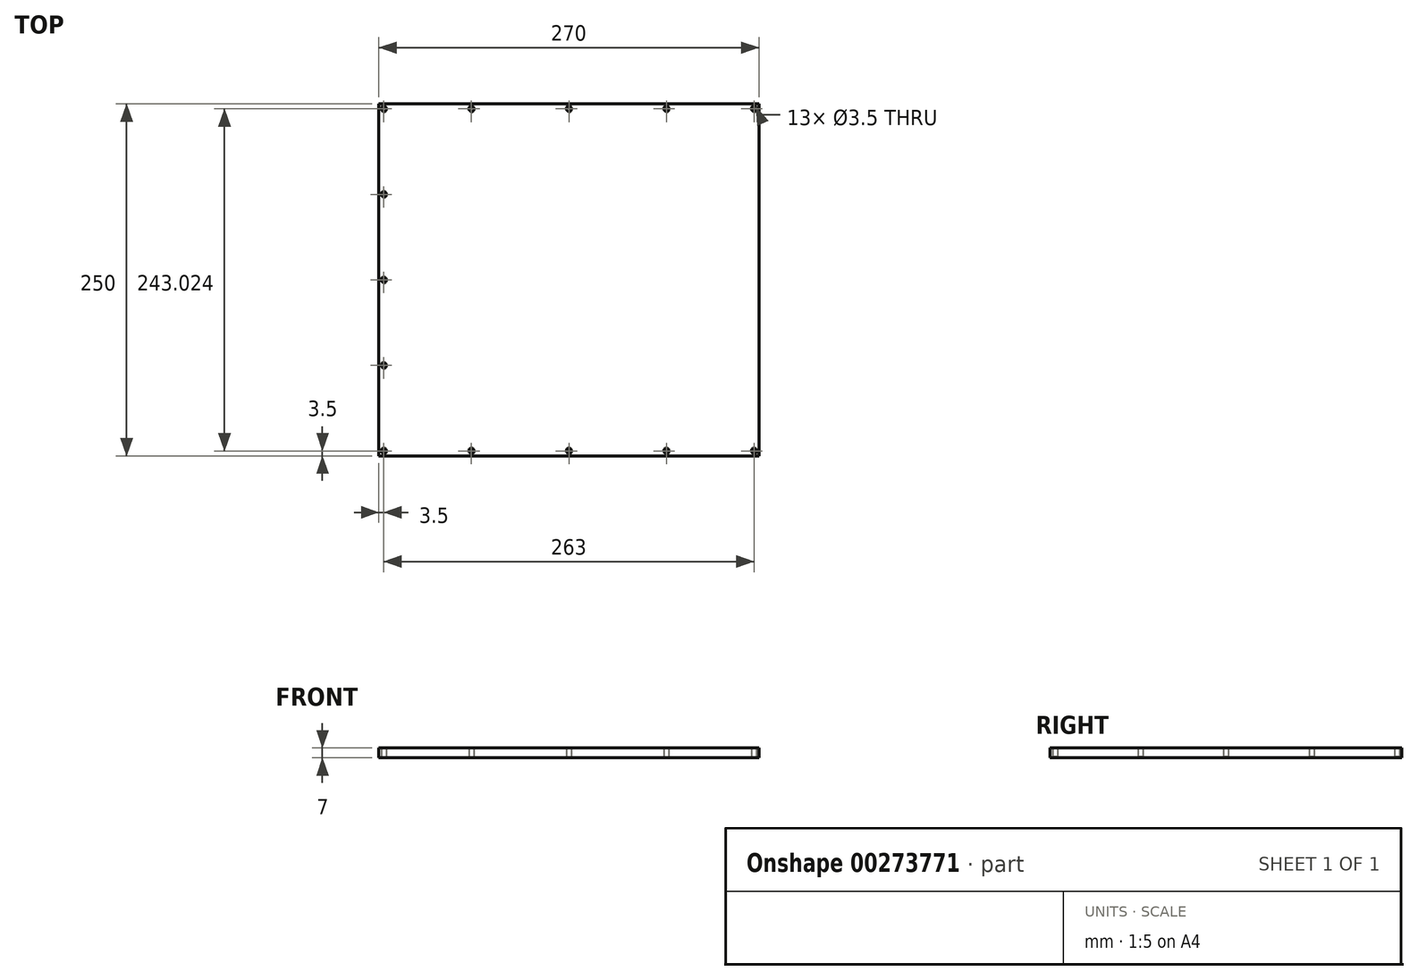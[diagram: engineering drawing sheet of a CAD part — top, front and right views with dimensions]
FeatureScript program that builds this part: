
annotation { "Feature Type Name" : "Feature", "Feature Type Description" : "" }
export const myFeature = defineFeature(function(context is Context, id is Id, definition is map)
    precondition{}
    {
        {
            var Q0;
            Q0=qCreatedBy(makeId("Top.planeOp"),FACE);
            var sketch = newSketch(context, id + "F0", { "sketchPlane" : qUnion([Q0])});
            skLineSegment(sketch, "E0.bottom", {"start": v(0, 0) * mm, "end": v(270, 0) * mm});
            skLineSegment(sketch, "E0.top", {"start": v(0, 250) * mm, "end": v(270, 250) * mm});
            skLineSegment(sketch, "E0.left", {"start": v(0, 0) * mm, "end": v(0, 250) * mm});
            skLineSegment(sketch, "E0.right", {"start": v(270, 0) * mm, "end": v(270, 250) * mm});
            skSolve(sketch);
        }
        {
            var Q0;
            Q0=qCreatedBy(makeId("Top.planeOp"),FACE);
            cPlane(context, id + "F1", {"entities" : qUnion([Q0]), "cplaneType" : CPlaneType.OFFSET, "offset" : 150 * mm, "oppositeDirection" : true, "width" : 150 * mm, "height" : 150 * mm});
        }
        {
            var Q0;
            Q0=qCreatedBy(id+"F1.planeOp",FACE);
            var sketch = newSketch(context, id + "F2", { "sketchPlane" : qUnion([Q0])});
            skLineSegment(sketch, "E1", {"start": v(0, -69.45) * mm, "end": v(0, 279.92) * mm});
            skSolve(sketch);
        }
        {
            var Q0;
            Q0=sQuery(id+"F2.wireOp",EDGE,"E1");
            cPlane(context, id + "F3", {"entities" : qUnion([Q0]), "cplaneType" : CPlaneType.LINE_ANGLE, "offset" : 25 * mm, "angle" : 10 * degree, "oppositeDirection" : true, "width" : 150 * mm, "height" : 150 * mm});
        }
        {
            var Q0;
            Q0=makeQuery(id+"F0.imprint","IMPRINT",FACE,{"disambiguationData":[TD([[makeQuery(id+"F0.imprint","IMPRINT",EDGE,{"derivedFrom":sQuery(id+"F0.wireOp",EDGE,"E0.bottom")}),1.0]])]});
            var Q1;
            Q1=qCreatedBy(id+"F3.planeOp",FACE);
            extrude(context, id + "F4", {"entities" : qUnion([Q0]), "endBound" : BoundingType.UP_TO_SURFACE, "oppositeDirection" : true, "endBoundEntityFace" : qUnion([Q1]), "depth" : 25 * mm});
        }
        {
            var Q0;
            Q0=makeQuery(id+"F4.opExtrude","CAP_FACE",FACE,{"disambiguationData":[OSD([sQuery(id+"F0.wireOp",EDGE,"E0.bottom"),sQuery(id+"F0.wireOp",EDGE,"E0.top"),sQuery(id+"F0.wireOp",EDGE,"E0.left"),sQuery(id+"F0.wireOp",EDGE,"E0.right")])],"isStart":true});
            var sketch = newSketch(context, id + "F5", { "sketchPlane" : qUnion([Q0])});
            skLineSegment(sketch, "E2.bottom", {"start": v(7, 243) * mm, "end": v(270, 243) * mm});
            skLineSegment(sketch, "E2.top", {"start": v(7, 7) * mm, "end": v(270, 7) * mm});
            skLineSegment(sketch, "E2.left", {"start": v(7, 243) * mm, "end": v(7, 7) * mm});
            skLineSegment(sketch, "E2.right", {"start": v(270, 243) * mm, "end": v(270, 7) * mm});
            skSolve(sketch);
        }
        {
            var Q0;
            Q0=makeQuery(id+"F5.imprint","IMPRINT",FACE,{"disambiguationData":[TD([[makeQuery(id+"F5.imprint","IMPRINT",EDGE,{"derivedFrom":sQuery(id+"F5.wireOp",EDGE,"E2.bottom")}),-1.0]])]});
            extrude(context, id + "F6", {"entities" : qUnion([Q0]), "operationType" : NewBodyOperationType.REMOVE, "oppositeDirection" : true, "depth" : 36 * mm});
        }
        {
            var Q0;
            Q0=makeQuery(id+"F4.opExtrude","SWEPT_FACE",FACE,{"disambiguationData":[OSD([sQuery(id+"F0.wireOp",EDGE,"E0.bottom")])]});
            var sketch = newSketch(context, id + "F7", { "sketchPlane" : qUnion([Q0])});
            skArc(sketch, "E3", {"start": v(216.53, -52.3) * mm, "mid": v(200.3, -75.47) * mm, "end": v(223.47, -91.7) * mm});
            skLineSegment(sketch, "E4", {"start": v(223.47, -91.7) * mm, "end": v(270, -83.5) * mm});
            skLineSegment(sketch, "E5", {"start": v(216.53, -52.3) * mm, "end": v(270, -42.88) * mm});
            skLineSegment(sketch, "E6", {"start": v(270, -42.88) * mm, "end": v(270, -83.5) * mm});
            skSolve(sketch);
        }
        {
            var Q0;
            Q0=makeQuery(id+"F7.imprint","IMPRINT",FACE,{"disambiguationData":[TD([[makeQuery(id+"F7.imprint","IMPRINT",EDGE,{"derivedFrom":sQuery(id+"F7.wireOp",EDGE,"E3")}),1.0]])]});
            var Q1;
            Q1=sQuery(id+"F7.wireOp",EDGE,"E5");
            var Q2;
            Q2=sQuery(id+"F7.wireOp",EDGE,"E3");
            var Q3;
            Q3=sQuery(id+"F7.wireOp",EDGE,"E4");
            var Q4;
            Q4=sQuery(id+"F7.wireOp",EDGE,"E6");
            extrude(context, id + "F8", {"entities" : qUnion([Q0]), "operationType" : NewBodyOperationType.REMOVE, "surfaceEntities" : qUnion([Q1, Q2, Q3, Q4]), "endBound" : BoundingType.THROUGH_ALL, "oppositeDirection" : true, "depth" : 25 * mm});
        }
        {
            var Q0;
            Q0=makeQuery(id+"F4.opExtrude","CAP_FACE",FACE,{"disambiguationData":[OSD([sQuery(id+"F0.wireOp",EDGE,"E0.bottom"),sQuery(id+"F0.wireOp",EDGE,"E0.top"),sQuery(id+"F0.wireOp",EDGE,"E0.left"),sQuery(id+"F0.wireOp",EDGE,"E0.right")])],"isStart":true});
            var sketch = newSketch(context, id + "F9", { "sketchPlane" : qUnion([Q0])});
            skPoint(sketch, "E7", {"position": v(65.75, 3.5) * mm});
            skPoint(sketch, "E8", {"position": v(3.5, 3.5) * mm});
            skPoint(sketch, "E9", {"position": v(3.5, 64.25) * mm});
            skPoint(sketch, "E10", {"position": v(3.5, 125) * mm});
            skPoint(sketch, "E11", {"position": v(3.5, 246.5) * mm});
            skPoint(sketch, "E12", {"position": v(3.5, 185.75) * mm});
            skPoint(sketch, "E13", {"position": v(135, 3.5) * mm});
            skPoint(sketch, "E14", {"position": v(135, 246.52) * mm});
            skPoint(sketch, "E15.MirrorP", {"position": v(65.75, 246.5) * mm});
            skPoint(sketch, "E16.MirrorP", {"position": v(204.25, 246.52) * mm});
            skPoint(sketch, "E17.MirrorP", {"position": v(266.5, 246.52) * mm});
            skPoint(sketch, "E18.MirrorP", {"position": v(266.5, 3.5) * mm});
            skPoint(sketch, "E19.MirrorP", {"position": v(204.25, 3.5) * mm});
            skSolve(sketch);
        }
        {
            var Q0;
            Q0=sQuery(id+"F9.wireOp",VERTEX,"E9");
            var Q1;
            Q1=sQuery(id+"F9.wireOp",VERTEX,"E10");
            var Q2;
            Q2=sQuery(id+"F9.wireOp",VERTEX,"E12");
            var Q3;
            Q3=sQuery(id+"F9.wireOp",VERTEX,"E11");
            var Q4;
            Q4=sQuery(id+"F9.wireOp",VERTEX,"E8");
            var Q5;
            Q5=sQuery(id+"F9.wireOp",VERTEX,"E7");
            var Q6;
            Q6=sQuery(id+"F9.wireOp",VERTEX,"E13");
            var Q7;
            Q7=sQuery(id+"F9.wireOp",VERTEX,"E19.MirrorP");
            var Q8;
            Q8=sQuery(id+"F9.wireOp",VERTEX,"E18.MirrorP");
            var Q9;
            Q9=sQuery(id+"F9.wireOp",VERTEX,"E17.MirrorP");
            var Q10;
            Q10=sQuery(id+"F9.wireOp",VERTEX,"E16.MirrorP");
            var Q11;
            Q11=sQuery(id+"F9.wireOp",VERTEX,"E14");
            var Q12;
            Q12=sQuery(id+"F9.wireOp",VERTEX,"E15.MirrorP");
            var Q13;
            Q13=makeQuery(id+"F4.opExtrude","SWEPT_BODY",BODY,{"disambiguationData":[OSD([sQuery(id+"F0.wireOp",EDGE,"E0.bottom"),sQuery(id+"F0.wireOp",EDGE,"E0.top"),sQuery(id+"F0.wireOp",EDGE,"E0.left"),sQuery(id+"F0.wireOp",EDGE,"E0.right")])]});
            hole(context, id + "F10", {"style" : HoleStyle.SIMPLE, "endStyle" : HoleEndStyle.BLIND, "standardTappedOrClearance" : lookupTablePath({ "standard" : "ISO", "size" : "3.5", "type" : "Drilled" }), "standardBlindInLast" : lookupTablePath({ "standard" : "ISO", "size" : "3.5", "type" : "Drilled" }), "holeDiameter" : 3.5 * mm, "holeDepth" : 12 * mm, "tappedDepth" : 12 * mm, "tapClearance" : 3, "locations" : qUnion([Q0, Q1, Q2, Q3, Q4, Q5, Q6, Q7, Q8, Q9, Q10, Q11, Q12]), "scope" : qUnion([Q13])});
        }
        {
            var Q0;
            Q0=makeQuery(id+"F4.opExtrude","CAP_FACE",FACE,{"disambiguationData":[OSD([sQuery(id+"F0.wireOp",EDGE,"E0.bottom"),sQuery(id+"F0.wireOp",EDGE,"E0.top"),sQuery(id+"F0.wireOp",EDGE,"E0.left"),sQuery(id+"F0.wireOp",EDGE,"E0.right")])],"isStart":true});
            var sketch = newSketch(context, id + "F11", { "sketchPlane" : qUnion([Q0])});
            skLineSegment(sketch, "E20.bottom", {"start": v(0, 250) * mm, "end": v(270, 250) * mm});
            skLineSegment(sketch, "E20.top", {"start": v(0, 0) * mm, "end": v(270, 0) * mm});
            skLineSegment(sketch, "E20.left", {"start": v(0, 250) * mm, "end": v(0, 0) * mm});
            skLineSegment(sketch, "E20.right", {"start": v(270, 250) * mm, "end": v(270, 0) * mm});
            skSolve(sketch);
        }
        {
            var Q0;
            {var subQ2=sQuery(id+"F11.wireOp",EDGE,"E20.bottom");Q0=makeQuery(id+"F11.imprint","IMPRINT",FACE,{"disambiguationData":[TD([[makeQuery(id+"F11.imprint","IMPRINT",EDGE,{"derivedFrom":subQ2}),-1.0]])]});}
            var sketch = newSketch(context, id + "F12", { "sketchPlane" : qUnion([Q0])});
            skCircle(sketch, "E21.0.0", {"center": v(266.5, 246.52) * mm, "radius": 1.75 * mm});
            skLineSegment(sketch, "E22.0.0", {"start": v(270, 7) * mm, "end": v(7, 7) * mm});
            skLineSegment(sketch, "E22.0.1", {"start": v(7, 7) * mm, "end": v(7, 243) * mm});
            skLineSegment(sketch, "E22.0.2", {"start": v(7, 243) * mm, "end": v(270, 243) * mm});
            skLineSegment(sketch, "E22.0.3", {"start": v(270, 243) * mm, "end": v(270, 250) * mm});
            skLineSegment(sketch, "E22.0.4", {"start": v(270, 250) * mm, "end": v(0, 250) * mm});
            skLineSegment(sketch, "E22.0.5", {"start": v(0, 250) * mm, "end": v(0, 0) * mm});
            skLineSegment(sketch, "E22.0.6", {"start": v(0, 0) * mm, "end": v(270, 0) * mm});
            skLineSegment(sketch, "E22.0.7", {"start": v(270, 0) * mm, "end": v(270, 7) * mm});
            skCircle(sketch, "E23.0", {"center": v(204.25, 246.52) * mm, "radius": 1.75 * mm});
            skCircle(sketch, "E24.0", {"center": v(135, 246.52) * mm, "radius": 1.75 * mm});
            skCircle(sketch, "E25.0", {"center": v(65.75, 246.5) * mm, "radius": 1.75 * mm});
            skCircle(sketch, "E26.0", {"center": v(3.5, 246.5) * mm, "radius": 1.75 * mm});
            skCircle(sketch, "E27.0", {"center": v(3.5, 185.75) * mm, "radius": 1.75 * mm});
            skCircle(sketch, "E28.0", {"center": v(3.5, 125) * mm, "radius": 1.75 * mm});
            skCircle(sketch, "E29.0", {"center": v(266.5, 3.5) * mm, "radius": 1.75 * mm});
            skCircle(sketch, "E30.0", {"center": v(204.25, 3.5) * mm, "radius": 1.75 * mm});
            skCircle(sketch, "E31.0", {"center": v(135, 3.5) * mm, "radius": 1.75 * mm});
            skCircle(sketch, "E32.0", {"center": v(65.75, 3.5) * mm, "radius": 1.75 * mm});
            skCircle(sketch, "E33.0", {"center": v(3.5, 64.25) * mm, "radius": 1.75 * mm});
            skCircle(sketch, "E34.0", {"center": v(3.5, 3.5) * mm, "radius": 1.75 * mm});
            skSolve(sketch);
        }
        {
            var Q0;
            {var subQ2=sQuery(id+"F11.wireOp",EDGE,"E20.bottom");Q0=makeQuery(id+"F11.imprint","IMPRINT",FACE,{"disambiguationData":[TD([[makeQuery(id+"F11.imprint","IMPRINT",EDGE,{"derivedFrom":subQ2}),-1.0]])]});}
            var sketch = newSketch(context, id + "F13", { "sketchPlane" : qUnion([Q0])});
            skPoint(sketch, "E35.0", {"position": v(270, 250) * mm});
            skLineSegment(sketch, "E36.bottom", {"start": v(270, 250) * mm, "end": v(0, 250) * mm});
            skLineSegment(sketch, "E36.top", {"start": v(270, 0) * mm, "end": v(0, 0) * mm});
            skLineSegment(sketch, "E36.left", {"start": v(270, 250) * mm, "end": v(270, 0) * mm});
            skLineSegment(sketch, "E36.right", {"start": v(0, 250) * mm, "end": v(0, 0) * mm});
            skSolve(sketch);
        }
        {
            var Q0;
            Q0 = qSketchRegion(id + "F13", true);
            extrude(context, id + "F14", {"entities" : qUnion([Q0]), "depth" : 7 * mm});
        }
        {
            var Q0;
            Q0=sQuery(id+"F12.wireOp",VERTEX,"E26.0.center");
            var Q1;
            Q1=sQuery(id+"F12.wireOp",VERTEX,"E25.0.center");
            var Q2;
            Q2=sQuery(id+"F12.wireOp",VERTEX,"E24.0.center");
            var Q3;
            Q3=sQuery(id+"F12.wireOp",VERTEX,"E23.0.center");
            var Q4;
            Q4=sQuery(id+"F12.wireOp",VERTEX,"E21.0.0.center");
            var Q5;
            Q5=sQuery(id+"F12.wireOp",VERTEX,"E27.0.center");
            var Q6;
            Q6=sQuery(id+"F12.wireOp",VERTEX,"E28.0.center");
            var Q7;
            Q7=sQuery(id+"F12.wireOp",VERTEX,"E33.0.center");
            var Q8;
            Q8=sQuery(id+"F12.wireOp",VERTEX,"E34.0.center");
            var Q9;
            Q9=sQuery(id+"F12.wireOp",VERTEX,"E32.0.center");
            var Q10;
            Q10=sQuery(id+"F12.wireOp",VERTEX,"E31.0.center");
            var Q11;
            Q11=sQuery(id+"F12.wireOp",VERTEX,"E30.0.center");
            var Q12;
            Q12=sQuery(id+"F12.wireOp",VERTEX,"E29.0.center");
            var Q13;
            Q13=makeQuery(id+"F14.opExtrude","SWEPT_BODY",BODY,{"disambiguationData":[OSD([sQuery(id+"F13.wireOp",EDGE,"E36.bottom"),sQuery(id+"F13.wireOp",EDGE,"E36.top"),sQuery(id+"F13.wireOp",EDGE,"E36.left"),sQuery(id+"F13.wireOp",EDGE,"E36.right")])]});
            hole(context, id + "F15", {"style" : HoleStyle.C_SINK, "endStyle" : HoleEndStyle.THROUGH, "oppositeDirection" : true, "standardTappedOrClearance" : lookupTablePath({ "standard" : "ISO", "size" : "3.5", "type" : "Drilled" }), "standardBlindInLast" : lookupTablePath({ "standard" : "ISO", "size" : "3.5", "type" : "Drilled" }), "holeDiameter" : 3.5 * mm, "cSinkDiameter" : 5 * mm, "cSinkAngle" : 90 * degree, "tappedDepth" : 12 * mm, "tapClearance" : 3, "locations" : qUnion([Q0, Q1, Q2, Q3, Q4, Q5, Q6, Q7, Q8, Q9, Q10, Q11, Q12]), "scope" : qUnion([Q13])});
        }
        {
            var Q0;
            Q0=makeQuery(id+"F4.opExtrude","SWEPT_BODY",BODY,{"disambiguationData":[OSD([sQuery(id+"F0.wireOp",EDGE,"E0.bottom"),sQuery(id+"F0.wireOp",EDGE,"E0.top"),sQuery(id+"F0.wireOp",EDGE,"E0.left"),sQuery(id+"F0.wireOp",EDGE,"E0.right")])]});
            deleteBodies(context, id + "F16", {"entities" : qUnion([Q0])});
        }
    });
